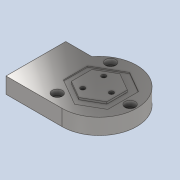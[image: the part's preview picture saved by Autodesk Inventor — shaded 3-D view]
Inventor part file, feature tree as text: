
AUTODESK INVENTOR PART (.ipt)
format: ipt  version: 2022 (Build 260153000, 153)  size: 168,960 bytes
history: native  units: in
note: dims shown in document units (in); Inventor stores cm internally (conversion verified against a paired STEP export)
features: sketch x3, extrude x3, hole x3, other x1
ambient origin geometry x8: Origin, YZ Plane, XZ Plane, XY Plane, X Axis, Y Axis, Z Axis, Center Point
bodies: Body1 (feature_tree)
feature tree (10):
  other  "ソリッド1"
  sketch  "スケッチ1"
  extrude  "押し出し1"  Depth=3.1496in
  hole  "穴3"  [1 undecoded]
  hole  "穴4"  [1 undecoded]
  extrude  "押し出し2"  Depth=2.3622in
  hole  "穴5"  [1 undecoded]
  extrude  "押し出し3"  Depth=2.5984in
  sketch  "スケッチ2"
  sketch  "スケッチ4"
note: 3 required parameter values undecoded (feature->parameter linkage not recoverable at this tier; creation-order binding heuristic only, values carry confidence <= 0.55)
